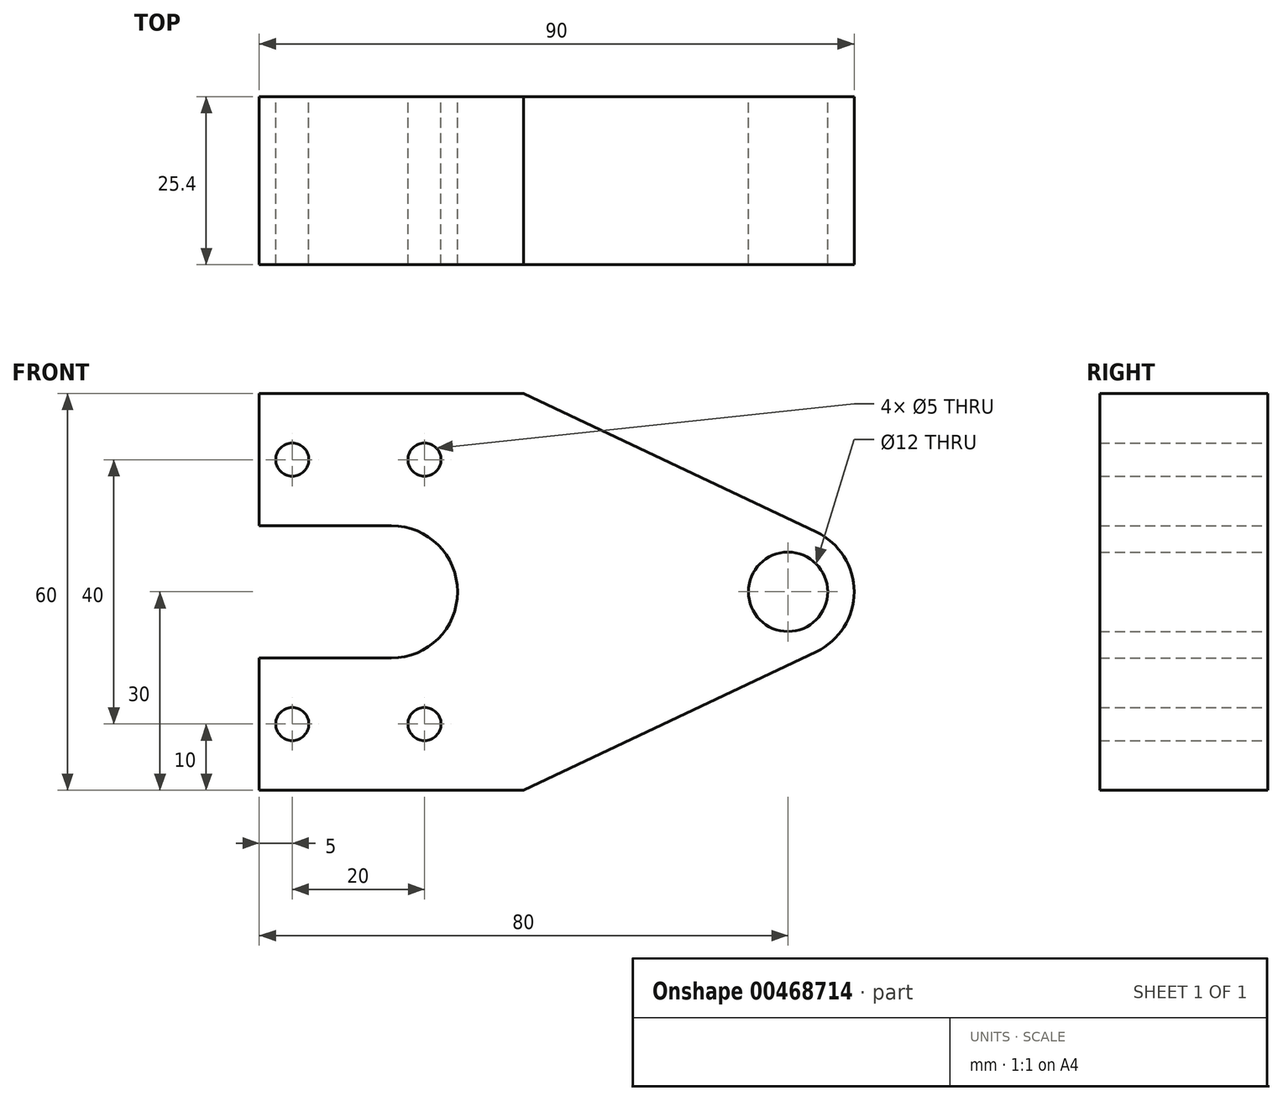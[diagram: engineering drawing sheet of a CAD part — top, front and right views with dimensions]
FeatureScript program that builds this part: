
annotation { "Feature Type Name" : "Feature", "Feature Type Description" : "" }
export const myFeature = defineFeature(function(context is Context, id is Id, definition is map)
    precondition{}
    {
        {
            var Q0;
            Q0=qCreatedBy(makeId("Front.planeOp"),FACE);
            var sketch = newSketch(context, id + "F0", { "sketchPlane" : qUnion([Q0])});
            skArc(sketch, "E0", {"start": v(0, -10) * mm, "mid": v(10, 0) * mm, "end": v(0, 10) * mm});
            skLineSegment(sketch, "E1", {"start": v(0, 10) * mm, "end": v(-20, 10) * mm});
            skLineSegment(sketch, "E2", {"start": v(0, -10) * mm, "end": v(-20, -10) * mm});
            skLineSegment(sketch, "E3", {"start": v(-20, -10) * mm, "end": v(-20, -30) * mm});
            skLineSegment(sketch, "E4", {"start": v(-20, 10) * mm, "end": v(-20, 30) * mm});
            skLineSegment(sketch, "E5", {"start": v(-20, 30) * mm, "end": v(20, 30) * mm});
            skLineSegment(sketch, "E6", {"start": v(-20, -30) * mm, "end": v(20, -30) * mm});
            skArc(sketch, "E7", {"start": v(64.28, -9.04) * mm, "mid": v(70, 0) * mm, "end": v(64.28, 9.04) * mm});
            skPoint(sketch, "E7.centerSnap0", {"position": v(60, -2.16) * mm});
            skLineSegment(sketch, "E8", {"start": v(20, 30) * mm, "end": v(64.28, 9.04) * mm});
            skLineSegment(sketch, "E9", {"start": v(20, -30) * mm, "end": v(64.28, -9.04) * mm});
            skPoint(sketch, "E10.startSnap0", {"position": v(-15, 20) * mm});
            skCircle(sketch, "E11", {"center": v(-15, 20) * mm, "radius": 2.5 * mm});
            skCircle(sketch, "E12", {"center": v(5, 20) * mm, "radius": 2.5 * mm});
            skCircle(sketch, "E13.MirrorC", {"center": v(-15, -20) * mm, "radius": 2.5 * mm});
            skCircle(sketch, "E14.MirrorC", {"center": v(5, -20) * mm, "radius": 2.5 * mm});
            skCircle(sketch, "E15", {"center": v(60, 0) * mm, "radius": 6 * mm});
            skSolve(sketch);
        }
        {
            var Q0;
            Q0=makeQuery(id+"F0.imprint","IMPRINT",FACE,{"disambiguationData":[TD([[makeQuery(id+"F0.imprint","IMPRINT",EDGE,{"derivedFrom":sQuery(id+"F0.wireOp",EDGE,"E0")}),-1.0]])]});
            extrude(context, id + "F1", {"entities" : qUnion([Q0]), "depth" : 25.4 * mm});
        }
    });
